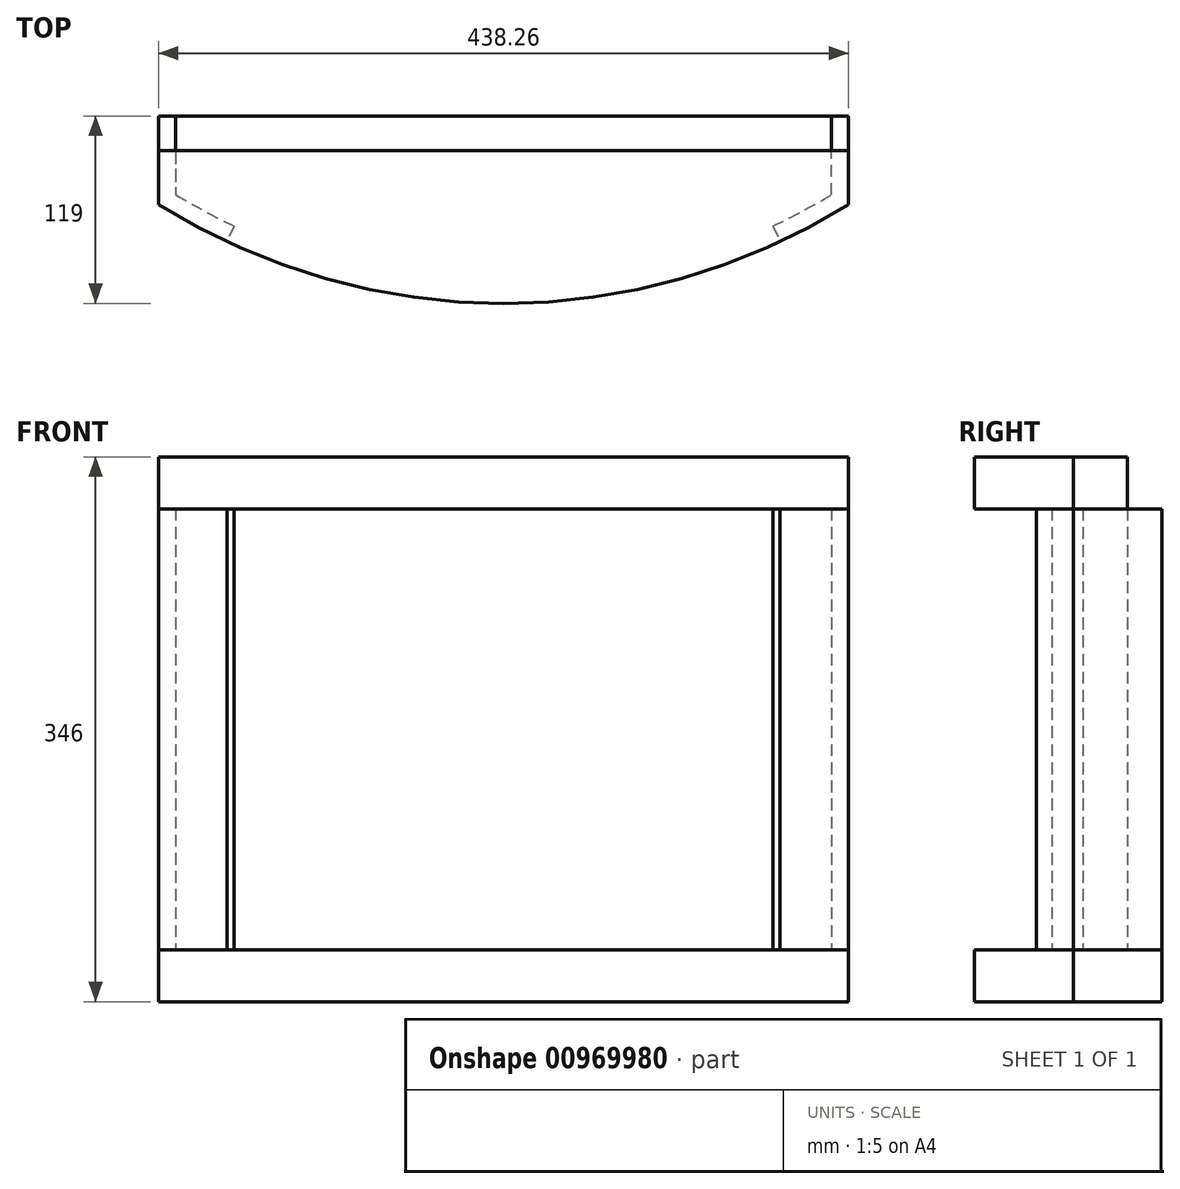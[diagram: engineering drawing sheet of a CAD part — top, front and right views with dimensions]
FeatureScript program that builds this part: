
annotation { "Feature Type Name" : "Feature", "Feature Type Description" : "" }
export const myFeature = defineFeature(function(context is Context, id is Id, definition is map)
    precondition{}
    {
        {
            var Q0;
            Q0=qCreatedBy(makeId("Top.planeOp"),FACE);
            var sketch = newSketch(context, id + "F0", { "sketchPlane" : qUnion([Q0])});
            skLineSegment(sketch, "E0", {"start": v(-219.13, 48.5) * mm, "end": v(219.13, 48.5) * mm});
            skLineSegment(sketch, "E1", {"start": v(-219.13, 48.5) * mm, "end": v(-219.13, 14.35) * mm});
            skLineSegment(sketch, "E2", {"start": v(219.13, 48.5) * mm, "end": v(219.13, 14.35) * mm});
            skArc(sketch, "E3", {"start": v(-219.13, 14.35) * mm, "mid": v(0, -48.5) * mm, "end": v(219.13, 14.35) * mm});
            skSolve(sketch);
        }
        {
            var Q0;
            Q0=makeQuery(id+"F0.imprint","IMPRINT",FACE,{"disambiguationData":[TD([[makeQuery(id+"F0.imprint","IMPRINT",EDGE,{"derivedFrom":sQuery(id+"F0.wireOp",EDGE,"E0")}),-1.0]])]});
            extrude(context, id + "F1", {"entities" : qUnion([Q0]), "depth" : 33 * mm, "offsetDistance" : 25 * mm});
        }
        {
            var Q0;
            Q0=makeQuery(id+"F1.opExtrude","CAP_FACE",FACE,{"disambiguationData":[OSD([sQuery(id+"F0.wireOp",EDGE,"E0"),sQuery(id+"F0.wireOp",EDGE,"E1"),sQuery(id+"F0.wireOp",EDGE,"E2"),sQuery(id+"F0.wireOp",EDGE,"E3")])],"isStart":true});
            cPlane(context, id + "F2", {"entities" : qUnion([Q0]), "cplaneType" : CPlaneType.OFFSET, "offset" : 280 * mm, "width" : 150 * mm, "height" : 150 * mm});
        }
        {
            var Q0;
            Q0=qCreatedBy(id+"F2.planeOp",FACE);
            var sketch = newSketch(context, id + "F3", { "sketchPlane" : qUnion([Q0])});
            skLineSegment(sketch, "E4.0.0", {"start": v(-219.13, -48.5) * mm, "end": v(-219.13, -14.35) * mm});
            skArc(sketch, "E4.0.1", {"start": v(-219.13, -14.35) * mm, "mid": v(0, 48.5) * mm, "end": v(219.13, -14.35) * mm});
            skLineSegment(sketch, "E4.0.2", {"start": v(219.13, -14.35) * mm, "end": v(219.13, -48.5) * mm});
            skLineSegment(sketch, "E4.0.3", {"start": v(219.13, -48.5) * mm, "end": v(-219.13, -48.5) * mm});
            skSolve(sketch);
        }
        {
            var Q0;
            Q0=makeQuery(id+"F3.imprint","IMPRINT",FACE,{"disambiguationData":[TD([[makeQuery(id+"F3.imprint","IMPRINT",EDGE,{"derivedFrom":sQuery(id+"F3.wireOp",EDGE,"E4.0.0")}),-1.0]])]});
            extrude(context, id + "F4", {"entities" : qUnion([Q0]), "depth" : 33 * mm, "offsetDistance" : 25 * mm});
        }
        {
            var Q0;
            Q0=makeQuery(id+"F4.opExtrude","SWEPT_FACE",FACE,{"disambiguationData":[OSD([sQuery(id+"F3.wireOp",EDGE,"E4.0.3")])]});
            extrude(context, id + "F5", {"entities" : qUnion([Q0]), "operationType" : NewBodyOperationType.ADD, "depth" : 22 * mm, "offsetDistance" : 25 * mm});
        }
        {
            var Q0;
            {var subQ0=sQuery(id+"F3.wireOp",EDGE,"E4.0.3");Q0=makeQuery(id+"F5.boolean.opBoolean","MERGE",FACE,{"derivedFrom":[makeQuery(id+"F4.opExtrude","CAP_FACE",FACE,{"disambiguationData":[OSD([sQuery(id+"F3.wireOp",EDGE,"E4.0.0"),sQuery(id+"F3.wireOp",EDGE,"E4.0.1"),sQuery(id+"F3.wireOp",EDGE,"E4.0.2"),subQ0])],"isStart":true}),makeQuery(id+"F5.opExtrude","SWEPT_FACE",FACE,{"disambiguationData":[OSD([subQ0]),TDD([makeQuery(id+"F4.opExtrude","CAP_EDGE",EDGE,{"disambiguationData":[OSD([subQ0])],"isStart":true})])]})]});}
            var sketch = newSketch(context, id + "F6", { "sketchPlane" : qUnion([Q0])});
            skLineSegment(sketch, "E5.0", {"start": v(219.13, 14.35) * mm, "end": v(219.13, 70.5) * mm});
            skLineSegment(sketch, "E6.0", {"start": v(-219.13, 70.5) * mm, "end": v(-219.13, 14.35) * mm});
            skArc(sketch, "E7.0", {"start": v(-219.13, 14.35) * mm, "mid": v(-197.76, 1.86) * mm, "end": v(-175.67, -9.32) * mm});
            skLineSegment(sketch, "E8.0", {"start": v(208.13, 20.5) * mm, "end": v(208.13, 70.5) * mm});
            skArc(sketch, "E8.1", {"start": v(-208.13, 20.5) * mm, "mid": v(-189.83, 10.08) * mm, "end": v(-171, 0.64) * mm});
            skLineSegment(sketch, "E8.2", {"start": v(-208.13, 70.5) * mm, "end": v(-208.13, 20.5) * mm});
            skLineSegment(sketch, "E9", {"start": v(-219.13, 70.5) * mm, "end": v(-208.13, 70.5) * mm});
            skLineSegment(sketch, "E10", {"start": v(208.13, 70.5) * mm, "end": v(219.13, 70.5) * mm});
            skLineSegment(sketch, "E11", {"start": v(0, 30.3) * mm, "end": v(0, -86.65) * mm});
            skPoint(sketch, "E11.endSnap0", {"position": v(0, -37.5) * mm});
            skLineSegment(sketch, "E12.0", {"start": v(-171, 0.64) * mm, "end": v(-171, -86.65) * mm, "construction": true});
            skLineSegment(sketch, "E13.0", {"start": v(171, 0.64) * mm, "end": v(171, -86.65) * mm, "construction": true});
            skLineSegment(sketch, "E14", {"start": v(-171, 0.64) * mm, "end": v(-175.67, -9.32) * mm});
            skLineSegment(sketch, "E15", {"start": v(171, 0.64) * mm, "end": v(175.67, -9.32) * mm});
            skArc(sketch, "E16.trimOffspring", {"start": v(175.67, -9.32) * mm, "mid": v(197.76, 1.86) * mm, "end": v(219.13, 14.35) * mm});
            skArc(sketch, "E17.trimOffspring", {"start": v(171, 0.64) * mm, "mid": v(189.83, 10.08) * mm, "end": v(208.13, 20.5) * mm});
            skSolve(sketch);
        }
        {
            var Q0;
            Q0 = qSketchRegion(id + "F6", true);
            extrude(context, id + "F7", {"entities" : qUnion([Q0]), "depth" : 280 * mm, "offsetDistance" : 25 * mm});
        }
        {
            var Q0;
            {var subQ0=sQuery(id+"F3.wireOp",EDGE,"E4.0.3");Q0=makeQuery(id+"F5.boolean.opBoolean","MERGE",FACE,{"derivedFrom":[makeQuery(id+"F4.opExtrude","CAP_FACE",FACE,{"disambiguationData":[OSD([sQuery(id+"F3.wireOp",EDGE,"E4.0.0"),sQuery(id+"F3.wireOp",EDGE,"E4.0.1"),sQuery(id+"F3.wireOp",EDGE,"E4.0.2"),subQ0])],"isStart":true}),makeQuery(id+"F5.opExtrude","SWEPT_FACE",FACE,{"disambiguationData":[OSD([subQ0]),TDD([makeQuery(id+"F4.opExtrude","CAP_EDGE",EDGE,{"disambiguationData":[OSD([subQ0])],"isStart":true})])]})]});}
            var sketch = newSketch(context, id + "F8", { "sketchPlane" : qUnion([Q0])});
            skLineSegment(sketch, "E18.0", {"start": v(-208.13, 70.5) * mm, "end": v(-208.13, 48.5) * mm});
            skLineSegment(sketch, "E19.0", {"start": v(208.13, 70.5) * mm, "end": v(-208.13, 70.5) * mm});
            skLineSegment(sketch, "E20.0", {"start": v(208.13, 48.5) * mm, "end": v(208.13, 70.5) * mm});
            skPoint(sketch, "E21.orphan", {"position": v(219.13, 70.5) * mm});
            skPoint(sketch, "E22.orphan", {"position": v(-219.13, 70.5) * mm});
            skLineSegment(sketch, "E23.0", {"start": v(208.13, 48.5) * mm, "end": v(-208.13, 48.5) * mm});
            skPoint(sketch, "E24.orphan", {"position": v(-208.13, 20.5) * mm});
            skPoint(sketch, "E25.orphan", {"position": v(208.13, 20.5) * mm});
            skSolve(sketch);
        }
        {
            var Q0;
            Q0=makeQuery(id+"F8.imprint","IMPRINT",FACE,{"disambiguationData":[TD([[makeQuery(id+"F8.imprint","IMPRINT",EDGE,{"derivedFrom":sQuery(id+"F8.wireOp",EDGE,"E18.0")}),1.0]])]});
            extrude(context, id + "F9", {"entities" : qUnion([Q0]), "depth" : 280 * mm, "offsetDistance" : 25 * mm});
        }
    });
